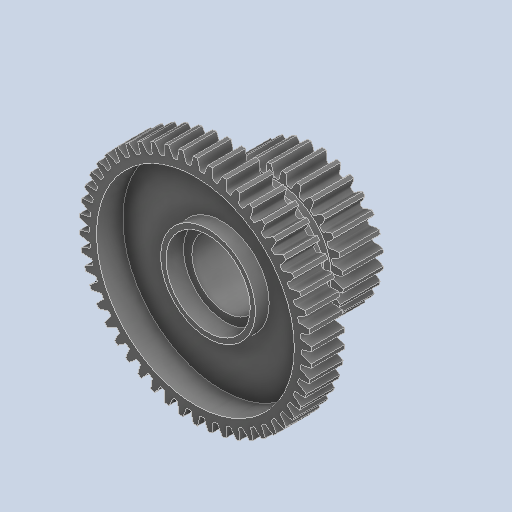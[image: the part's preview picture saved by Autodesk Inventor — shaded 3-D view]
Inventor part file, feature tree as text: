
AUTODESK INVENTOR PART (.ipt)
format: ipt  version: 2024.2 (Build 282272000, 272)  size: 733,184 bytes
history: native  units: in
note: dims shown in document units (in); Inventor stores cm internally (conversion verified against a paired STEP export)
features: chamfer x1
ambient origin geometry x8: Origin, YZ Plane, XZ Plane, XY Plane, X Axis, Y Axis, Z Axis, Center Point
bodies: Solid1 (feature_tree)
feature tree (1):
  chamfer  "Chamfer1"  [1 undecoded]
note: 1 required parameter value undecoded (feature->parameter linkage not recoverable at this tier; creation-order binding heuristic only, values carry confidence <= 0.55)
